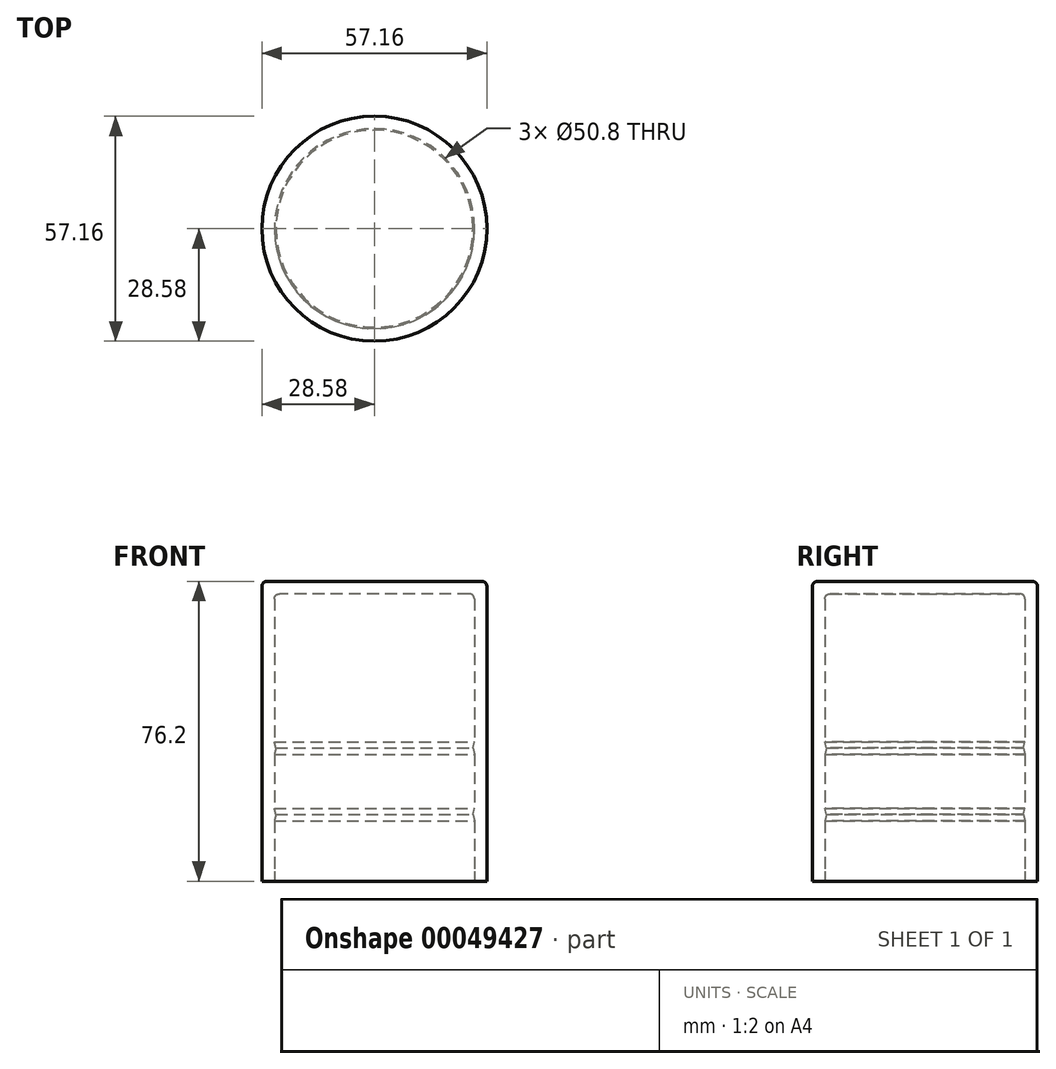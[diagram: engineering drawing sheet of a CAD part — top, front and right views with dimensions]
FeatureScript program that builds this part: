
annotation { "Feature Type Name" : "Feature", "Feature Type Description" : "" }
export const myFeature = defineFeature(function(context is Context, id is Id, definition is map)
    precondition{}
    {
        {
            assignVariable(context, id + "F0", {"name" : "friction_point", "anyValue" : 0.01});
        }
        {
            var Q0;
            Q0=qCreatedBy(makeId("Front.planeOp"),FACE);
            var sketch = newSketch(context, id + "F1", { "sketchPlane" : qUnion([Q0])});
            skLineSegment(sketch, "E0", {"start": v(0, 76.2) * mm, "end": v(-28.58, 76.2) * mm});
            skLineSegment(sketch, "E1", {"start": v(-28.58, 76.2) * mm, "end": v(-28.57, 0) * mm});
            skLineSegment(sketch, "E2", {"start": v(-28.57, 0) * mm, "end": v(-25.4, 0) * mm});
            skLineSegment(sketch, "E3", {"start": v(-25.4, 0) * mm, "end": v(-25.4, 15.35) * mm});
            skLineSegment(sketch, "E4", {"start": v(-25.4, 18.52) * mm, "end": v(-25.02, 16.93) * mm});
            skLineSegment(sketch, "E5", {"start": v(-25.02, 16.93) * mm, "end": v(-25.4, 15.35) * mm});
            skLineSegment(sketch, "E6", {"start": v(-25.4, 32.28) * mm, "end": v(-25.02, 33.87) * mm});
            skLineSegment(sketch, "E7", {"start": v(-25.02, 33.87) * mm, "end": v(-25.4, 35.45) * mm});
            skLineSegment(sketch, "E8", {"start": v(-25.4, 35.45) * mm, "end": v(-25.4, 73.03) * mm});
            skLineSegment(sketch, "E9", {"start": v(-25.4, 73.03) * mm, "end": v(0, 73.03) * mm});
            skLineSegment(sketch, "E10", {"start": v(0, 73.03) * mm, "end": v(0, 76.2) * mm});
            skLineSegment(sketch, "E11", {"start": v(-25.4, 18.52) * mm, "end": v(-25.4, 32.28) * mm});
            skSolve(sketch);
        }
        {
            var Q0;
            Q0=makeQuery(id+"F1.imprint","IMPRINT",FACE,{"disambiguationData":[TD([[makeQuery(id+"F1.imprint","IMPRINT",EDGE,{"derivedFrom":sQuery(id+"F1.wireOp",EDGE,"E0")}),1.0]])]});
            var Q1;
            Q1=sQuery(id+"F1.wireOp",EDGE,"E10");
            revolve(context, id + "F2", {"entities" : qUnion([Q0]), "axis" : qUnion([Q1]), "revolveType" : RevolveType.FULL});
        }
        {
            var Q0;
            Q0=makeQuery(id+"F2.opRevolve","SWEPT_EDGE",EDGE,{"disambiguationData":[OSD([sQuery(id+"F1.wireOp",EDGE,"E0"),sQuery(id+"F1.wireOp",EDGE,"E1")])]});
            var Q1;
            Q1=makeQuery(id+"F2.opRevolve","SWEPT_EDGE",EDGE,{"disambiguationData":[OSD([sQuery(id+"F1.wireOp",EDGE,"E8"),sQuery(id+"F1.wireOp",EDGE,"E9")])]});
            fillet(context, id + "F3", {"entities" : qUnion([Q0, Q1]), "radius" : 1.27 * mm, "tangentPropagation" : true, "allowEdgeOverflow" : false});
        }
        {
            var Q0;
            Q0=makeQuery(id+"F2.opRevolve","SWEPT_EDGE",EDGE,{"disambiguationData":[OSD([sQuery(id+"F1.wireOp",EDGE,"E2"),sQuery(id+"F1.wireOp",EDGE,"E3")])]});
            chamfer(context, id + "F4", {"entities" : qUnion([Q0]), "chamferType" : ChamferType.TWO_OFFSETS, "width1" : 2.54 * mm, "oppositeDirection" : false, "width2" : (getVariable(context, 'friction_point')) * mm, "tangentPropagation" : true});
        }
    });
